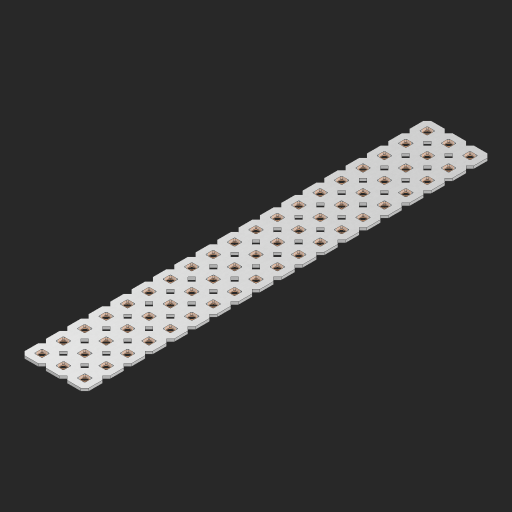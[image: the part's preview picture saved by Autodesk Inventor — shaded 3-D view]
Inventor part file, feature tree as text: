
AUTODESK INVENTOR PART (.ipt)
format: ipt  version: 2023 (Build 270158000, 158)  size: 936,448 bytes
history: native  units: in
note: dims shown in document units (in); Inventor stores cm internally (conversion verified against a paired STEP export)
features: other x58, extrude x56, sketch x2, pattern_linear x1
ambient origin geometry x8: Origin, YZ Plane, XZ Plane, XY Plane, X Axis, Y Axis, Z Axis, Center Point
bodies: Solid1 (feature_tree), Body (feature_tree)
feature tree (117):
  pattern_linear  "Rectangular Pattern1"  Spacing1=0.09in  [1 undecoded]
  sketch  "Sketch1"  dims[d1=0.5in]
  sketch  "Sketch2"  dims[d2=0.182in d3=0.09in d4=0.09in d5=0.09in d6=0.09in d7=0.09in d8=0.09in d9=0.09in d10=0.09in d11=0.02in d13=0.0in d14=0.172in d15=0.0625in d16=0.0in d19=0.5in d22=0.5in]
  other  "Srf1"
  other  "Srf126"
  other  "Srf127"
  other  "Srf128"
  other  "Srf129"
  other  "Srf130"
  other  "Srf131"
  other  "Srf250"
  other  "Srf251"
  other  "Srf252"
  other  "Srf253"
  other  "Srf254"
  other  "Srf255"
  other  "Srf256"
  other  "Srf257"
  other  "Srf258"
  other  "Srf259"
  other  "Srf260"
  other  "Srf261"
  other  "Srf268"
  other  "Srf269"
  other  "Srf270"
  other  "Srf271"
  other  "Srf272"
  other  "Srf273"
  other  "Srf274"
  other  "Srf275"
  other  "Srf276"
  other  "Srf277"
  other  "Srf278"
  other  "Srf279"
  other  "Srf280"
  other  "Srf281"
  other  "Srf282"
  other  "Srf283"
  other  "Srf284"
  other  "Srf285"
  other  "Srf286"
  other  "Srf293"
  other  "Srf294"
  other  "Srf295"
  other  "Srf296"
  other  "Srf297"
  other  "Srf298"
  other  "Srf299"
  other  "Srf300"
  other  "Srf301"
  other  "Srf302"
  other  "Srf303"
  other  "Srf304"
  other  "Srf305"
  other  "Srf306"
  other  "Srf307"
  other  "Srf308"
  other  "Srf309"
  other  "Srf310"
  other  "Srf311"
  other  "Circle"
  extrude  "ExtrusionSrf126"  Depth=0.09in
  extrude  "ExtrusionSrf127"  Depth=0.09in
  extrude  "ExtrusionSrf128"  Depth=0.09in
  extrude  "ExtrusionSrf129"  Depth=0.09in
  extrude  "ExtrusionSrf130"  Depth=0.09in
  extrude  "ExtrusionSrf131"  Depth=0.09in
  extrude  "ExtrusionSrf250"  Depth=0.09in
  extrude  "ExtrusionSrf251"  Depth=0.02in
  extrude  "ExtrusionSrf252"  TaperAngle=0.0deg  [1 undecoded]
  extrude  "ExtrusionSrf253"  Depth=0.5in
  extrude  "ExtrusionSrf254"  Depth=0.0625in TaperAngle=0.0deg
  extrude  "ExtrusionSrf255"  Depth=0.5in
  extrude  "ExtrusionSrf256"  Depth=0.5in
  extrude  "ExtrusionSrf257"  [1 undecoded]
  extrude  "ExtrusionSrf258"  [1 undecoded]
  extrude  "ExtrusionSrf259"  [1 undecoded]
  extrude  "ExtrusionSrf260"  [1 undecoded]
  extrude  "ExtrusionSrf261"  [1 undecoded]
  extrude  "ExtrusionSrf268"  [1 undecoded]
  extrude  "ExtrusionSrf269"  [1 undecoded]
  extrude  "ExtrusionSrf270"  [1 undecoded]
  extrude  "ExtrusionSrf271"  [1 undecoded]
  extrude  "ExtrusionSrf272"  [1 undecoded]
  extrude  "ExtrusionSrf273"  [1 undecoded]
  extrude  "ExtrusionSrf274"  [1 undecoded]
  extrude  "ExtrusionSrf275"  [1 undecoded]
  extrude  "ExtrusionSrf276"  [1 undecoded]
  extrude  "ExtrusionSrf277"  [1 undecoded]
  extrude  "ExtrusionSrf278"  [1 undecoded]
  extrude  "ExtrusionSrf279"  [1 undecoded]
  extrude  "ExtrusionSrf280"  [1 undecoded]
  extrude  "ExtrusionSrf281"  [1 undecoded]
  extrude  "ExtrusionSrf282"  [1 undecoded]
  extrude  "ExtrusionSrf283"  [1 undecoded]
  extrude  "ExtrusionSrf284"  [1 undecoded]
  extrude  "ExtrusionSrf285"  [1 undecoded]
  extrude  "ExtrusionSrf286"  [1 undecoded]
  extrude  "ExtrusionSrf293"  [1 undecoded]
  extrude  "ExtrusionSrf294"  [1 undecoded]
  extrude  "ExtrusionSrf295"  [1 undecoded]
  extrude  "ExtrusionSrf296"  [1 undecoded]
  extrude  "ExtrusionSrf297"  [1 undecoded]
  extrude  "ExtrusionSrf298"  [1 undecoded]
  extrude  "ExtrusionSrf299"  [1 undecoded]
  extrude  "ExtrusionSrf300"  [1 undecoded]
  extrude  "ExtrusionSrf301"  [1 undecoded]
  extrude  "ExtrusionSrf302"  [1 undecoded]
  extrude  "ExtrusionSrf303"  [1 undecoded]
  extrude  "ExtrusionSrf304"  [1 undecoded]
  extrude  "ExtrusionSrf305"  [1 undecoded]
  extrude  "ExtrusionSrf306"  [1 undecoded]
  extrude  "ExtrusionSrf307"  [1 undecoded]
  extrude  "ExtrusionSrf308"  [1 undecoded]
  extrude  "ExtrusionSrf309"  [1 undecoded]
  extrude  "ExtrusionSrf310"  [1 undecoded]
  extrude  "ExtrusionSrf311"  [1 undecoded]
note: 45 required parameter values undecoded (feature->parameter linkage not recoverable at this tier; creation-order binding heuristic only, values carry confidence <= 0.55)
